# Revit family: Скамейка бетонная «Сколково» без спинки Арт 12134
name_source: partatom
category: Антураж
revit_build: Autodesk Revit 2018 (Build: 20180423_1000(x64)
units: mm (PartAtom-declared; Revit-internal decimal feet)

## family parameters
Всегда вертикально = Да
Источник визуального образа = Геометрия семейства
На основе рабочей плоскости = Нет
Общий = Нет
При загрузке вырезать с полостями = Нет
Точка расчета площади = Нет

## types (2) — shared parameters
URL = https://hobbyka.ru
Артикул товара = Арт. 12134
Высота = 454 мм
Группа модели = Скамейки
Длина = 1800 мм
Длина настила = 1838 мм
Изготовитель = ООО «Хоббика»
Цвет настила = Дерево
Цвет основания = Бетон
Ширина = 500 мм

## per-type parameters (varying)
| type | Блок Бетон | Блок Бетон-дерево | Высота ББ | Изображение типоразмера | Материал изделия |
| Скамейка бетонная «Сколково» без спинки. Блок Бетон | Да | Нет | 454 мм | Скамейка бетонная «Сколково» без спинки Арт 12134 Блок бетон.jpeg | Бетон |
| Скамейка бетонная «Сколково» без спинки. Блок Бетон-дерево | Нет | Да | 300 мм | Скамейка бетонная «Сколково» без спинки Арт 12134 Блок бетон-дерево.jpeg | Бетон, дерево |

note: column(s) folded — value = type name in every type: Описание
